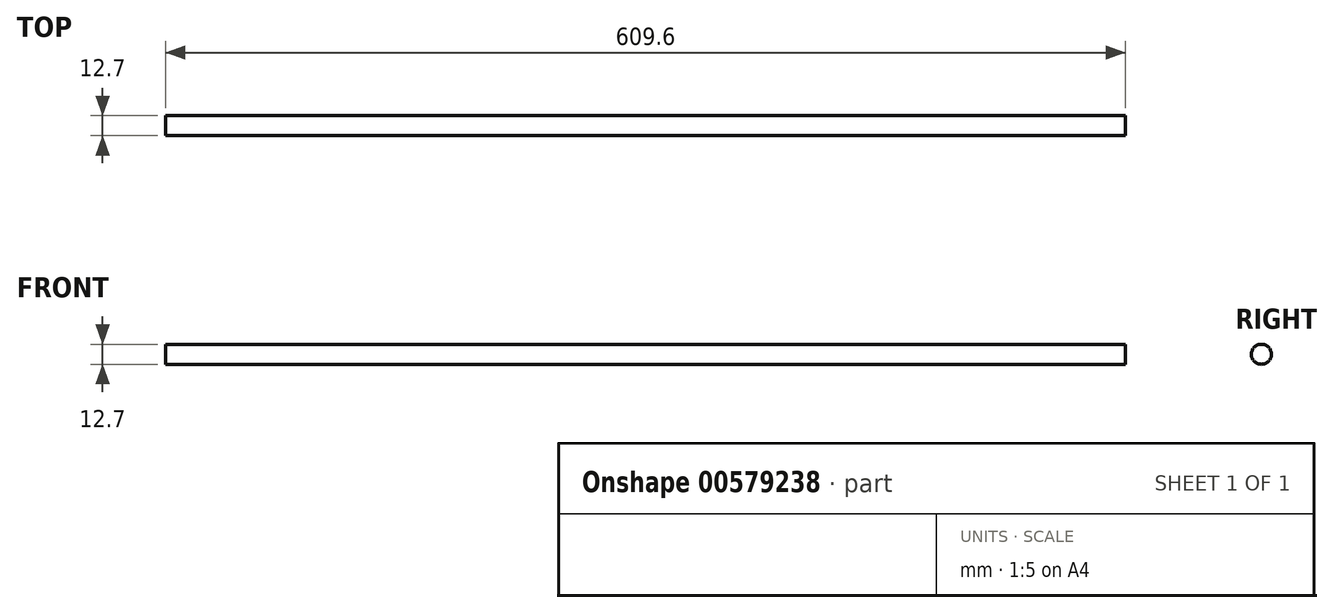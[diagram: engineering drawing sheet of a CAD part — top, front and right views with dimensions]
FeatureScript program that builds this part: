
annotation { "Feature Type Name" : "Feature", "Feature Type Description" : "" }
export const myFeature = defineFeature(function(context is Context, id is Id, definition is map)
    precondition{}
    {
        {
            var Q0;
            Q0=qCreatedBy(makeId("Front.planeOp"),FACE);
            var sketch = newSketch(context, id + "F0", { "sketchPlane" : qUnion([Q0])});
            skLineSegment(sketch, "E0.bottom", {"start": v(304.8, 6.35) * mm, "end": v(-304.8, 6.35) * mm});
            skLineSegment(sketch, "E0.top", {"start": v(304.8, -6.35) * mm, "end": v(-304.8, -6.35) * mm});
            skLineSegment(sketch, "E0.left", {"start": v(304.8, 6.35) * mm, "end": v(304.8, -6.35) * mm});
            skLineSegment(sketch, "E0.right", {"start": v(-304.8, 6.35) * mm, "end": v(-304.8, -6.35) * mm});
            skPoint(sketch, "E0.middle", {"position": v(0, 0) * mm});
            skLineSegment(sketch, "E1", {"start": v(-304.8, 0) * mm, "end": v(304.8, 0) * mm});
            skSolve(sketch);
        }
        {
            var Q0;
            Q0 = qSketchRegion(id + "F0", true);
            var Q1;
            Q1=sQuery(id+"F0.wireOp",EDGE,"E0.bottom");
            var Q2;
            Q2=sQuery(id+"F0.wireOp",EDGE,"E1");
            revolve(context, id + "F1", {"bodyType" : ToolBodyType.SURFACE, "entities" : qUnion([Q0]), "surfaceEntities" : qUnion([Q1]), "axis" : qUnion([Q2]), "revolveType" : RevolveType.ONE_DIRECTION, "angle" : 360 * degree});
        }
    });
